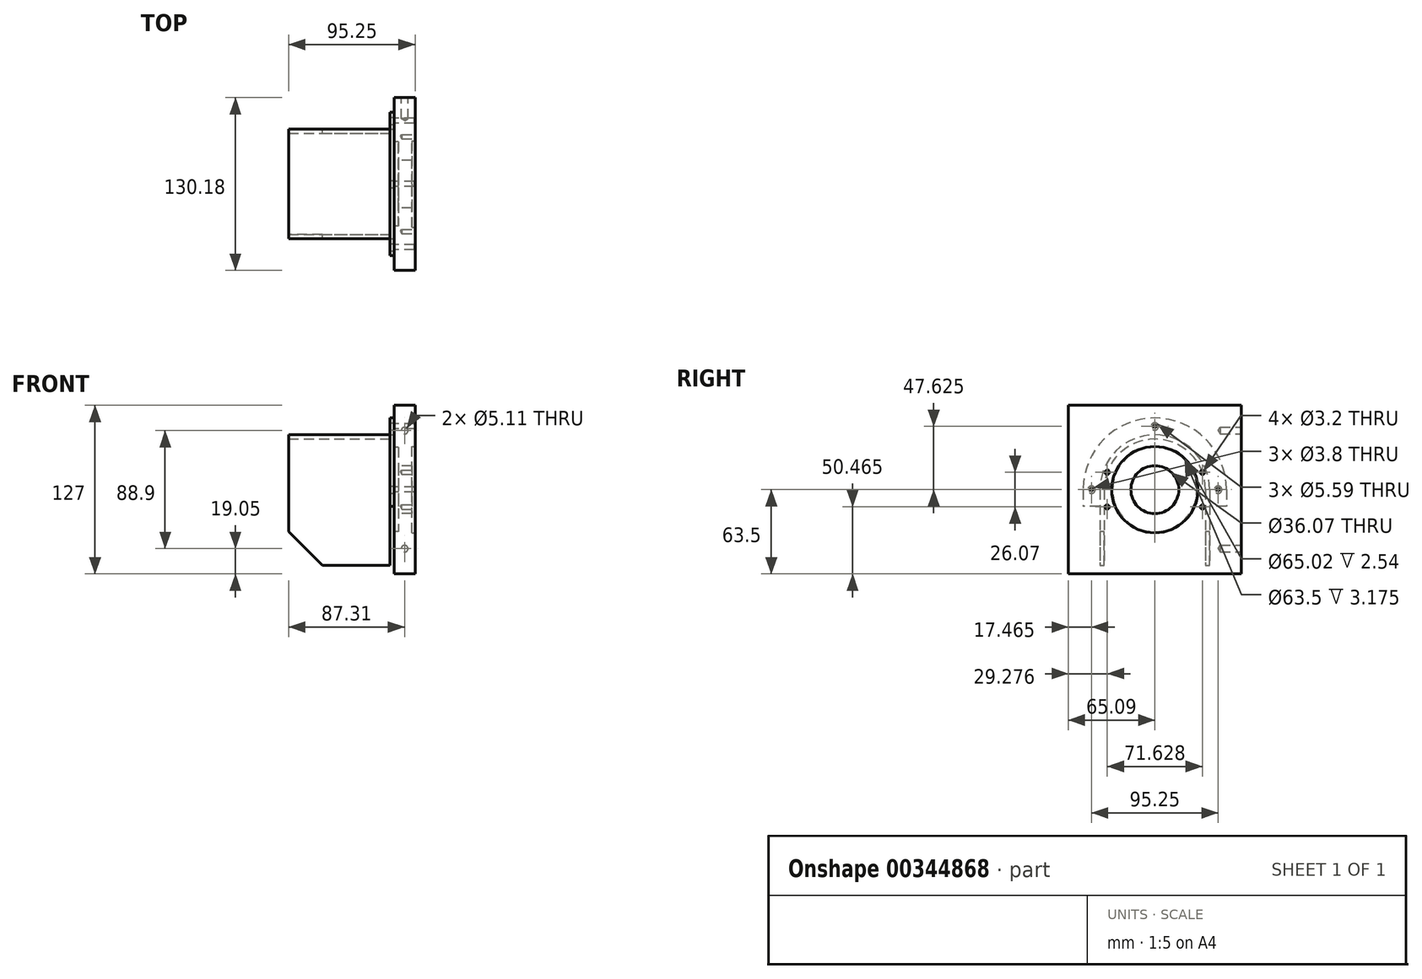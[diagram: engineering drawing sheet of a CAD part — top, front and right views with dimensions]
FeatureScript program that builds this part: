
annotation { "Feature Type Name" : "Feature", "Feature Type Description" : "" }
export const myFeature = defineFeature(function(context is Context, id is Id, definition is map)
    precondition{}
    {
        {
            var Q0;
            Q0=qCreatedBy(makeId("Right.planeOp"),FACE);
            var sketch = newSketch(context, id + "F0", { "sketchPlane" : qUnion([Q0])});
            skLineSegment(sketch, "E0.bottom", {"start": v(-65.09, 63.5) * mm, "end": v(65.09, 63.5) * mm});
            skLineSegment(sketch, "E0.top", {"start": v(-65.09, -63.5) * mm, "end": v(65.09, -63.5) * mm});
            skLineSegment(sketch, "E0.left", {"start": v(-65.09, 63.5) * mm, "end": v(-65.09, -63.5) * mm});
            skLineSegment(sketch, "E0.right", {"start": v(65.09, 63.5) * mm, "end": v(65.09, -63.5) * mm});
            skPoint(sketch, "E0.middle", {"position": v(0, 0) * mm});
            skCircle(sketch, "E1", {"center": v(0, 0) * mm, "radius": 18.03 * mm});
            skSolve(sketch);
        }
        {
            var Q0;
            Q0 = qSketchRegion(id + "F0", true);
            extrude(context, id + "F1", {"entities" : qUnion([Q0]), "endBound" : BoundingType.SYMMETRIC, "depth" : 15.88 * mm});
        }
        {
            var Q0;
            Q0=makeQuery(id+"F1.opExtrude","CAP_FACE",FACE,{"disambiguationData":[OSD([sQuery(id+"F0.wireOp",EDGE,"E0.bottom"),sQuery(id+"F0.wireOp",EDGE,"E0.top"),sQuery(id+"F0.wireOp",EDGE,"E0.left"),sQuery(id+"F0.wireOp",EDGE,"E0.right"),sQuery(id+"F0.wireOp",EDGE,"E1")])],"isStart":false});
            var sketch = newSketch(context, id + "F2", { "sketchPlane" : qUnion([Q0])});
            skCircle(sketch, "E2", {"center": v(0, 0) * mm, "radius": 32.51 * mm});
            skSolve(sketch);
        }
        {
            var Q0;
            Q0 = qSketchRegion(id + "F2", true);
            extrude(context, id + "F3", {"entities" : qUnion([Q0]), "operationType" : NewBodyOperationType.REMOVE, "oppositeDirection" : true, "depth" : 2.54 * mm});
        }
        {
            var Q0;
            Q0=makeQuery(id+"F1.opExtrude","CAP_FACE",FACE,{"disambiguationData":[OSD([sQuery(id+"F0.wireOp",EDGE,"E0.bottom"),sQuery(id+"F0.wireOp",EDGE,"E0.top"),sQuery(id+"F0.wireOp",EDGE,"E0.left"),sQuery(id+"F0.wireOp",EDGE,"E0.right"),sQuery(id+"F0.wireOp",EDGE,"E1")])],"isStart":false});
            var sketch = newSketch(context, id + "F4", { "sketchPlane" : qUnion([Q0])});
            skLineSegment(sketch, "E3", {"start": v(0, 0) * mm, "end": v(-88.38, 32.17) * mm, "construction": true});
            skLineSegment(sketch, "E4.MirrorCS", {"start": v(0, 0) * mm, "end": v(-88.38, -32.17) * mm, "construction": true});
            skLineSegment(sketch, "E5", {"start": v(0, 90.39) * mm, "end": v(0, -103) * mm, "construction": true});
            skPoint(sketch, "E5.endSnap0", {"position": v(0, 63.5) * mm});
            skLineSegment(sketch, "E6.0", {"start": v(-35.81, 90.39) * mm, "end": v(-35.81, -103) * mm, "construction": true});
            skPoint(sketch, "E7", {"position": v(-35.81, 13.04) * mm});
            skPoint(sketch, "E8", {"position": v(-35.81, -13.04) * mm});
            skPoint(sketch, "E9.MirrorP", {"position": v(35.81, 13.04) * mm});
            skPoint(sketch, "E10.MirrorP", {"position": v(35.81, -13.04) * mm});
            skSolve(sketch);
        }
        {
            var Q0;
            Q0=sQuery(id+"F4.wireOp",VERTEX,"E7");
            var Q1;
            Q1=sQuery(id+"F4.wireOp",VERTEX,"E8");
            var Q2;
            Q2=sQuery(id+"F4.wireOp",VERTEX,"E9.MirrorP");
            var Q3;
            Q3=sQuery(id+"F4.wireOp",VERTEX,"E10.MirrorP");
            var Q4;
            Q4=makeQuery(id+"F1.opExtrude","SWEPT_BODY",BODY,{"disambiguationData":[OSD([sQuery(id+"F0.wireOp",EDGE,"E0.bottom"),sQuery(id+"F0.wireOp",EDGE,"E0.top"),sQuery(id+"F0.wireOp",EDGE,"E0.left"),sQuery(id+"F0.wireOp",EDGE,"E0.right"),sQuery(id+"F0.wireOp",EDGE,"E1")])]});
            hole(context, id + "F5", {"style" : HoleStyle.SIMPLE, "endStyle" : HoleEndStyle.BLIND, "standardTappedOrClearance" : lookupTablePath({ "standard" : "ISO", "engagement" : "75%", "pitch" : "0.75 mm", "size" : "M4", "type" : "Tapped" }), "standardBlindInLast" : lookupTablePath({ "standard" : "ISO", "engagement" : "75%", "pitch" : "0.75 mm", "size" : "M4", "type" : "Tapped" }), "holeDiameter" : 3.2 * mm, "showTappedDepth" : true, "holeDepth" : 10 * mm, "isTappedThrough" : true, "tappedDepth" : 7.75 * mm, "tapClearance" : 3, "locations" : qUnion([Q0, Q1, Q2, Q3]), "scope" : qUnion([Q4])});
        }
        {
            var Q0;
            Q0=makeQuery(id+"F1.opExtrude","SWEPT_FACE",FACE,{"disambiguationData":[OSD([sQuery(id+"F0.wireOp",EDGE,"E0.right")])]});
            var sketch = newSketch(context, id + "F6", { "sketchPlane" : qUnion([Q0])});
            skLineSegment(sketch, "E11", {"start": v(0, 88.1) * mm, "end": v(0, -90.11) * mm, "construction": true});
            skLineSegment(sketch, "E12.0", {"start": v(-7.94, 63.5) * mm, "end": v(7.94, 63.5) * mm, "construction": true});
            skLineSegment(sketch, "E13.0", {"start": v(-7.94, 44.45) * mm, "end": v(7.94, 44.45) * mm, "construction": true});
            skLineSegment(sketch, "E14.0", {"start": v(-7.94, -44.45) * mm, "end": v(7.94, -44.45) * mm, "construction": true});
            skPoint(sketch, "E15", {"position": v(0, 44.45) * mm});
            skPoint(sketch, "E16", {"position": v(0, -44.45) * mm});
            skSolve(sketch);
        }
        {
            var Q0;
            Q0=sQuery(id+"F6.wireOp",VERTEX,"E15");
            var Q1;
            Q1=sQuery(id+"F6.wireOp",VERTEX,"E16");
            var Q2;
            Q2=makeQuery(id+"F1.opExtrude","SWEPT_BODY",BODY,{"disambiguationData":[OSD([sQuery(id+"F0.wireOp",EDGE,"E0.bottom"),sQuery(id+"F0.wireOp",EDGE,"E0.top"),sQuery(id+"F0.wireOp",EDGE,"E0.left"),sQuery(id+"F0.wireOp",EDGE,"E0.right"),sQuery(id+"F0.wireOp",EDGE,"E1")])]});
            hole(context, id + "F7", {"style" : HoleStyle.SIMPLE, "endStyle" : HoleEndStyle.BLIND, "standardTappedOrClearance" : lookupTablePath({ "standard" : "ANSI", "engagement" : "75%", "pitch" : "20 tpi", "size" : "1/4", "type" : "Tapped" }), "standardBlindInLast" : lookupTablePath({ "standard" : "ANSI", "engagement" : "75%", "pitch" : "20 tpi", "size" : "1/4", "type" : "Tapped" }), "holeDiameter" : 5.1 * mm, "showTappedDepth" : true, "holeDepth" : 15.88 * mm, "isTappedThrough" : true, "tappedDepth" : 12.06 * mm, "tapClearance" : 3, "locations" : qUnion([Q0, Q1]), "scope" : qUnion([Q2]), "majorDiameter" : 6.35 * mm});
        }
        {
            var Q0;
            Q0=makeQuery(id+"F1.opExtrude","CAP_FACE",FACE,{"disambiguationData":[OSD([sQuery(id+"F0.wireOp",EDGE,"E0.bottom"),sQuery(id+"F0.wireOp",EDGE,"E0.top"),sQuery(id+"F0.wireOp",EDGE,"E0.left"),sQuery(id+"F0.wireOp",EDGE,"E0.right"),sQuery(id+"F0.wireOp",EDGE,"E1")])],"isStart":true});
            cPlane(context, id + "F8", {"entities" : qUnion([Q0]), "cplaneType" : CPlaneType.OFFSET, "offset" : 3.17 * mm, "width" : 152.4 * mm, "height" : 152.4 * mm});
        }
        {
            var Q0;
            Q0=qCreatedBy(id+"F8.planeOp",FACE);
            var sketch = newSketch(context, id + "F9", { "sketchPlane" : qUnion([Q0])});
            skArc(sketch, "E17", {"start": v(41.28, 0) * mm, "mid": v(0, 41.28) * mm, "end": v(-41.28, 0) * mm});
            skLineSegment(sketch, "E18", {"start": v(0, 0) * mm, "end": v(-41.28, 0) * mm, "construction": true});
            skLineSegment(sketch, "E19", {"start": v(-41.28, 0) * mm, "end": v(-41.28, -57.15) * mm});
            skLineSegment(sketch, "E20", {"start": v(0, 107.75) * mm, "end": v(0, -88.09) * mm, "construction": true});
            skLineSegment(sketch, "E21.MirrorCS", {"start": v(41.28, 0) * mm, "end": v(41.28, -57.15) * mm});
            skLineSegment(sketch, "E22.0", {"start": v(-38.1, 0) * mm, "end": v(-38.1, -57.15) * mm});
            skArc(sketch, "E22.1", {"start": v(38.1, 0) * mm, "mid": v(0, 38.1) * mm, "end": v(-38.1, 0) * mm});
            skLineSegment(sketch, "E22.2", {"start": v(38.1, 0) * mm, "end": v(38.1, -57.15) * mm});
            skLineSegment(sketch, "E23", {"start": v(-41.28, -57.15) * mm, "end": v(-38.1, -57.15) * mm});
            skLineSegment(sketch, "E24", {"start": v(38.1, -57.15) * mm, "end": v(41.28, -57.15) * mm});
            skSolve(sketch);
        }
        {
            var Q0;
            Q0 = qSketchRegion(id + "F9", true);
            extrude(context, id + "F10", {"entities" : qUnion([Q0]), "depth" : 76.2 * mm});
        }
        {
            var Q0;
            Q0=makeQuery(id+"F10.opExtrude","CAP_EDGE",EDGE,{"disambiguationData":[OSD([sQuery(id+"F9.wireOp",EDGE,"E23")])],"isStart":false});
            var Q1;
            Q1=makeQuery(id+"F10.opExtrude","CAP_EDGE",EDGE,{"disambiguationData":[OSD([sQuery(id+"F9.wireOp",EDGE,"E24")])],"isStart":false});
            chamfer(context, id + "F11", {"entities" : qUnion([Q0, Q1]), "width" : 25.4 * mm, "tangentPropagation" : true});
        }
        {
            var Q0;
            Q0=makeQuery(id+"F1.opExtrude","CAP_FACE",FACE,{"disambiguationData":[OSD([sQuery(id+"F0.wireOp",EDGE,"E0.bottom"),sQuery(id+"F0.wireOp",EDGE,"E0.top"),sQuery(id+"F0.wireOp",EDGE,"E0.left"),sQuery(id+"F0.wireOp",EDGE,"E0.right"),sQuery(id+"F0.wireOp",EDGE,"E1")])],"isStart":true});
            var sketch = newSketch(context, id + "F12", { "sketchPlane" : qUnion([Q0])});
            skArc(sketch, "E25", {"start": v(53.98, 0) * mm, "mid": v(0, 53.98) * mm, "end": v(-53.98, 0) * mm});
            skLineSegment(sketch, "E26", {"start": v(-96.3, 0) * mm, "end": v(0, 0) * mm, "construction": true});
            skLineSegment(sketch, "E27.0", {"start": v(-53.98, -12.7) * mm, "end": v(-41.28, -12.7) * mm});
            skLineSegment(sketch, "E28", {"start": v(-53.98, 0) * mm, "end": v(-53.98, -12.7) * mm});
            skLineSegment(sketch, "E29", {"start": v(0, 90.56) * mm, "end": v(0, -109.74) * mm, "construction": true});
            skPoint(sketch, "E29.endSnap0", {"position": v(0, -63.5) * mm});
            skLineSegment(sketch, "E30.MirrorCS", {"start": v(53.98, 0) * mm, "end": v(53.98, -12.7) * mm});
            skArc(sketch, "E31.0", {"start": v(41.28, 0) * mm, "mid": v(0, 41.28) * mm, "end": v(-41.28, 0) * mm});
            skLineSegment(sketch, "E32.0", {"start": v(-41.28, 0) * mm, "end": v(-41.28, -12.7) * mm});
            skLineSegment(sketch, "E33.0", {"start": v(41.28, 0) * mm, "end": v(41.28, -12.7) * mm});
            skPoint(sketch, "E34.orphan", {"position": v(-41.28, -31.75) * mm});
            skLineSegment(sketch, "E35.trimOffspring", {"start": v(41.28, -12.7) * mm, "end": v(53.98, -12.7) * mm});
            skPoint(sketch, "E36.orphan", {"position": v(41.28, -31.75) * mm});
            skPoint(sketch, "E37.orphan", {"position": v(53.98, -93.86) * mm});
            skPoint(sketch, "E38.orphan", {"position": v(-53.98, -93.86) * mm});
            skLineSegment(sketch, "E39.trimOffspring", {"start": v(41.28, 0) * mm, "end": v(53.98, 0) * mm, "construction": true});
            skPoint(sketch, "E40", {"position": v(47.63, 0) * mm});
            skCircle(sketch, "E41", {"center": v(0, 0) * mm, "radius": 47.63 * mm, "construction": true});
            skPoint(sketch, "E42", {"position": v(0, 47.63) * mm});
            skPoint(sketch, "E43", {"position": v(-47.63, 0) * mm});
            skCircle(sketch, "E44", {"center": v(47.63, 0) * mm, "radius": 2.8 * mm});
            skCircle(sketch, "E45", {"center": v(0, 47.63) * mm, "radius": 2.8 * mm});
            skCircle(sketch, "E46", {"center": v(-47.63, 0) * mm, "radius": 2.8 * mm});
            skSolve(sketch);
        }
        {
            var Q0;
            Q0 = qSketchRegion(id + "F12", true);
            extrude(context, id + "F13", {"entities" : qUnion([Q0]), "depth" : 3.17 * mm});
        }
        {
            var Q0;
            Q0=makeQuery(id+"F1.opExtrude","CAP_FACE",FACE,{"disambiguationData":[OSD([sQuery(id+"F0.wireOp",EDGE,"E0.bottom"),sQuery(id+"F0.wireOp",EDGE,"E0.top"),sQuery(id+"F0.wireOp",EDGE,"E0.left"),sQuery(id+"F0.wireOp",EDGE,"E0.right"),sQuery(id+"F0.wireOp",EDGE,"E1")])],"isStart":true});
            var sketch = newSketch(context, id + "F14", { "sketchPlane" : qUnion([Q0])});
            skPoint(sketch, "E47.0", {"position": v(0, 47.63) * mm});
            skPoint(sketch, "E48.0", {"position": v(47.63, 0) * mm});
            skPoint(sketch, "E49.0", {"position": v(-47.63, 0) * mm});
            skSolve(sketch);
        }
        {
            var Q0;
            Q0=sQuery(id+"F14.wireOp",VERTEX,"E48.0");
            var Q1;
            Q1=sQuery(id+"F14.wireOp",VERTEX,"E47.0");
            var Q2;
            Q2=sQuery(id+"F14.wireOp",VERTEX,"E49.0");
            var Q3;
            Q3=makeQuery(id+"F1.opExtrude","SWEPT_BODY",BODY,{"disambiguationData":[OSD([sQuery(id+"F0.wireOp",EDGE,"E0.bottom"),sQuery(id+"F0.wireOp",EDGE,"E0.top"),sQuery(id+"F0.wireOp",EDGE,"E0.left"),sQuery(id+"F0.wireOp",EDGE,"E0.right"),sQuery(id+"F0.wireOp",EDGE,"E1")])]});
            hole(context, id + "F15", {"style" : HoleStyle.SIMPLE, "endStyle" : HoleEndStyle.BLIND, "standardTappedOrClearance" : lookupTablePath({ "standard" : "ANSI", "engagement" : "75%", "pitch" : "24 tpi", "size" : "#10", "type" : "Tapped" }), "standardBlindInLast" : lookupTablePath({ "standard" : "ANSI", "engagement" : "75%", "pitch" : "24 tpi", "size" : "#10", "type" : "Tapped" }), "holeDiameter" : 3.8 * mm, "showTappedDepth" : true, "holeDepth" : 15.24 * mm, "isTappedThrough" : true, "tappedDepth" : 12.06 * mm, "tapClearance" : 3, "locations" : qUnion([Q0, Q1, Q2]), "scope" : qUnion([Q3]), "majorDiameter" : 4.83 * mm});
        }
        {
            var Q0;
            Q0=makeQuery(id+"F12.imprint","IMPRINT",FACE,{"disambiguationData":[TD([[makeQuery(id+"F12.imprint","IMPRINT",EDGE,{"derivedFrom":sQuery(id+"F12.wireOp",EDGE,"E25")}),-1.0]])]});
            var sketch = newSketch(context, id + "F16", { "sketchPlane" : qUnion([Q0])});
            skCircle(sketch, "E50", {"center": v(0, 0) * mm, "radius": 31.75 * mm});
            skSolve(sketch);
        }
        {
            var Q0;
            Q0 = qSketchRegion(id + "F16", true);
            extrude(context, id + "F17", {"entities" : qUnion([Q0]), "operationType" : NewBodyOperationType.REMOVE, "oppositeDirection" : true, "depth" : 3.17 * mm});
        }
    });
